# Revit family: Deckel für 90 Vertikalbogen, fallend, Seitenhöhe 35
name_source: partatom
category: Generic Models
revit_build: Autodesk Revit 2015 (Build: 20140606_1530(x64)
units: mm (PartAtom-declared; Revit-internal decimal feet)

## types (3) — shared parameters
Manufacturer = OBO Bettermann
Material = Strip-galvanised
URL = http://www.obo-bettermann.com

## per-type parameters (varying)
| type | GTIN | Manufacturer Art.No. | Width | Width 1 |
| DBV 35 100 F FS | 4012195711902 | 7130764 | 100 mm  [stored 0.328084 ft] | 50 mm  [stored 0.164042 ft] |
| DBV 35 200 F FS | 4012195711940 | 7130772 | 200 mm  [stored 0.656168 ft] | 100 mm  [stored 0.328084 ft] |
| DBV 35 300 F FS | 4012195711957 | 7130776 | 300 mm | 150 mm |

note: column(s) folded — value = type name in every type: Article Type

note: [stored X ft] marks values corroborated as IEEE doubles in the binary element streams (Revit-internal decimal feet)

## geometry (parser evidence)
native form markers: Sweep x2
no freeform markers — native parametric forms only
